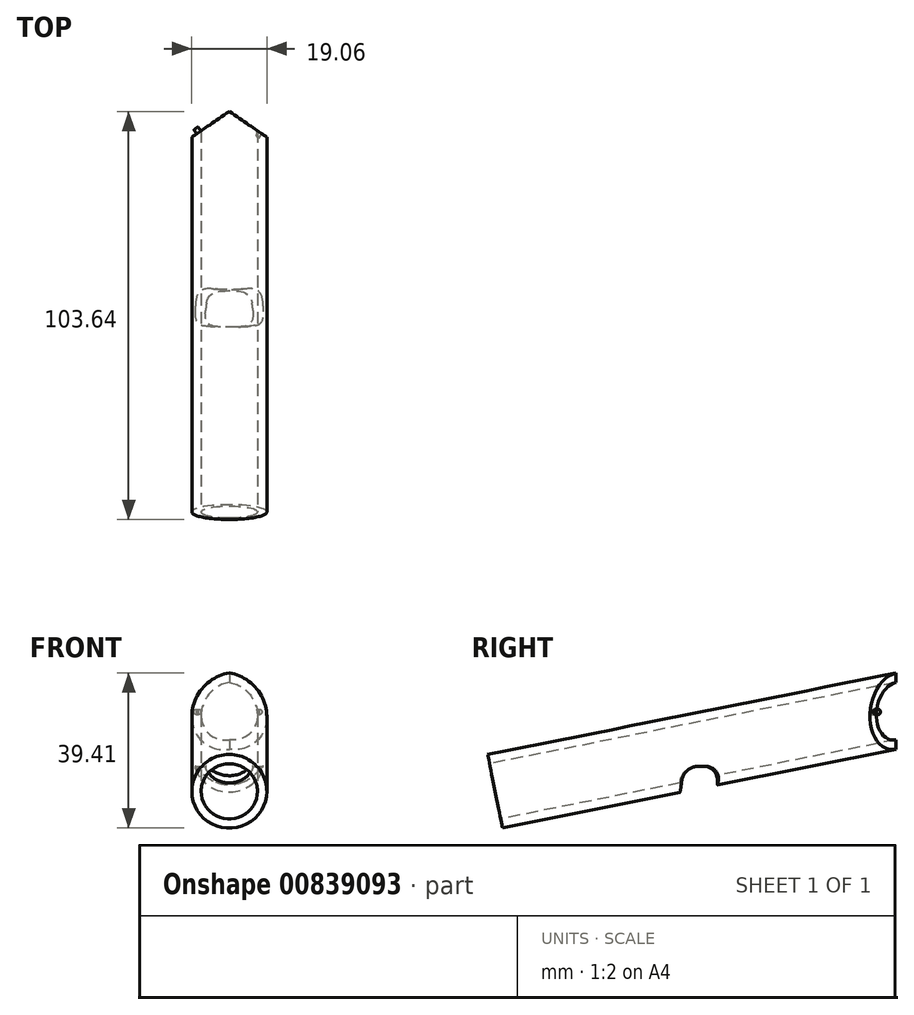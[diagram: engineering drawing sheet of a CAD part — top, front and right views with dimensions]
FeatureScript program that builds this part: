
annotation { "Feature Type Name" : "Feature", "Feature Type Description" : "" }
export const myFeature = defineFeature(function(context is Context, id is Id, definition is map)
    precondition{}
    {
        {
            var Q0;
            Q0=qCreatedBy(makeId("Front.planeOp"),FACE);
            var sketch = newSketch(context, id + "F0", { "sketchPlane" : qUnion([Q0])});
            skLineSegment(sketch, "E0", {"start": v(-25.47, 0) * mm, "end": v(29.78, 0) * mm});
            skSolve(sketch);
        }
        {
            var Q0;
            Q0=sQuery(id+"F0.wireOp",EDGE,"E0");
            cPlane(context, id + "F1", {"entities" : qUnion([Q0]), "cplaneType" : CPlaneType.LINE_ANGLE, "offset" : 25.4 * mm, "angle" : 11.3 * degree, "width" : 152.4 * mm, "height" : 152.4 * mm});
        }
        {
            var Q0;
            Q0=qCreatedBy(id+"F1.planeOp",FACE);
            var sketch = newSketch(context, id + "F2", { "sketchPlane" : qUnion([Q0])});
            skCircle(sketch, "E1", {"center": v(0, 0) * mm, "radius": 7.14 * mm});
            skCircle(sketch, "E2", {"center": v(0, 0) * mm, "radius": 9.53 * mm});
            skSolve(sketch);
        }
        {
            var Q0;
            Q0=makeQuery(id+"F2.imprint","IMPRINT",FACE,{"disambiguationData":[TD([[makeQuery(id+"F2.imprint","IMPRINT",EDGE,{"derivedFrom":sQuery(id+"F2.wireOp",EDGE,"E1")}),-1.0]])]});
            extrude(context, id + "F3", {"entities" : qUnion([Q0]), "depth" : 107.95 * mm, "offsetDistance" : 25.4 * mm});
        }
        {
            var Q0;
            Q0=qCreatedBy(makeId("Top.planeOp"),FACE);
            var sketch = newSketch(context, id + "F4", { "sketchPlane" : qUnion([Q0])});
            skLineSegment(sketch, "E3", {"start": v(0, 0) * mm, "end": v(0, 139.91) * mm, "construction": true});
            skLineSegment(sketch, "E4", {"start": v(-27.69, 95.25) * mm, "end": v(29.95, 95.25) * mm, "construction": true});
            skLineSegment(sketch, "E5", {"start": v(-9.52, 95.25) * mm, "end": v(-9.53, 133.35) * mm});
            skLineSegment(sketch, "E6", {"start": v(-9.53, 133.35) * mm, "end": v(9.52, 133.35) * mm});
            skLineSegment(sketch, "E7", {"start": v(9.52, 133.35) * mm, "end": v(9.52, 95.25) * mm});
            skLineSegment(sketch, "E8", {"start": v(0, 101.77) * mm, "end": v(-23.24, 85.86) * mm});
            skLineSegment(sketch, "E9", {"start": v(0, 101.77) * mm, "end": v(16.46, 90.5) * mm});
            skSolve(sketch);
        }
        {
            var Q0;
            Q0=qSketchRegion(id+"F4",true);
            extrude(context, id + "F5", {"entities" : qUnion([Q0]), "operationType" : NewBodyOperationType.REMOVE, "depth" : 127 * mm, "offsetDistance" : 25.4 * mm});
        }
        {
            var Q0;
            Q0=qCreatedBy(makeId("Right.planeOp"),FACE);
            var sketch = newSketch(context, id + "F6", { "sketchPlane" : qUnion([Q0])});
            skLineSegment(sketch, "E10", {"start": v(0, 0) * mm, "end": v(63.5, 0) * mm, "construction": true});
            skLineSegment(sketch, "E11", {"start": v(63.5, 0) * mm, "end": v(63.5, 10.16) * mm, "construction": true});
            skSolve(sketch);
        }
        {
            var Q0;
            Q0=qCreatedBy(makeId("Top.planeOp"),FACE);
            var sketch = newSketch(context, id + "F7", { "sketchPlane" : qUnion([Q0])});
            skCircle(sketch, "E12", {"center": v(0, 101.6) * mm, "radius": 54.61 * mm});
            skCircle(sketch, "E13", {"center": v(0, 101.6) * mm, "radius": 45.09 * mm});
            skSolve(sketch);
        }
        {
            var Q0;
            Q0=makeQuery(id+"F7.imprint","IMPRINT",FACE,{"disambiguationData":[TD([[makeQuery(id+"F7.imprint","IMPRINT",EDGE,{"derivedFrom":sQuery(id+"F7.wireOp",EDGE,"E12")}),1.0]])]});
            extrude(context, id + "F8", {"entities" : qUnion([Q0]), "operationType" : NewBodyOperationType.REMOVE, "depth" : 6.35 * mm, "offsetDistance" : 25.4 * mm, "hasSecondDirection" : true, "secondDirectionOppositeDirection" : true, "secondDirectionDepth" : 25.4 * mm});
        }
        {
            var Q0;
            Q0=makeQuery(id+"F8.boolean.opBoolean","COPY",EDGE,{"disambiguationData":[OD(0.0)],"derivedFrom":makeQuery(id+"F8.opExtrude","CAP_EDGE",EDGE,{"disambiguationData":[OSD([sQuery(id+"F7.wireOp",EDGE,"E13")])],"isStart":false})});
            var Q1;
            Q1=makeQuery(id+"F8.boolean.opBoolean","COPY",EDGE,{"disambiguationData":[OD(1.0)],"derivedFrom":makeQuery(id+"F8.opExtrude","CAP_EDGE",EDGE,{"disambiguationData":[OSD([sQuery(id+"F7.wireOp",EDGE,"E12")])],"isStart":false})});
            var Q2;
            Q2=makeQuery(id+"F8.boolean.opBoolean","COPY",EDGE,{"disambiguationData":[OD(1.0)],"derivedFrom":makeQuery(id+"F8.opExtrude","CAP_EDGE",EDGE,{"disambiguationData":[OSD([sQuery(id+"F7.wireOp",EDGE,"E13")])],"isStart":false})});
            var Q3;
            Q3=makeQuery(id+"F8.boolean.opBoolean","COPY",EDGE,{"disambiguationData":[OD(0.0)],"derivedFrom":makeQuery(id+"F8.opExtrude","CAP_EDGE",EDGE,{"disambiguationData":[OSD([sQuery(id+"F7.wireOp",EDGE,"E12")])],"isStart":false})});
            fillet(context, id + "F9", {"entities" : qUnion([Q0, Q1, Q2, Q3]), "radius" : 3.8 * mm, "tangentPropagation" : true, "allowEdgeOverflow" : false});
        }
        {
            var Q0;
            Q0=makeQuery(id+"F5.boolean.opBoolean","COPY",FACE,{"derivedFrom":makeQuery(id+"F5.opExtrude","SWEPT_FACE",FACE,{"disambiguationData":[OSD([sQuery(id+"F4.wireOp",EDGE,"E9")])]})});
            var sketch = newSketch(context, id + "F10", { "sketchPlane" : qUnion([Q0])});
            skCircle(sketch, "E14", {"center": v(48.1, 20.17) * mm, "radius": 0.64 * mm});
            skSolve(sketch);
        }
        {
            var Q0;
            Q0=makeQuery(id+"F10.imprint","IMPRINT",FACE,{"disambiguationData":[TD([[makeQuery(id+"F10.imprint","IMPRINT",EDGE,{"derivedFrom":sQuery(id+"F10.wireOp",EDGE,"E14")}),1.0]])]});
            extrude(context, id + "F11", {"entities" : qUnion([Q0]), "operationType" : NewBodyOperationType.REMOVE, "oppositeDirection" : true, "depth" : 1.27 * mm, "offsetDistance" : 25.4 * mm});
        }
        {
            var Q0;
            Q0=makeQuery(id+"F5.boolean.opBoolean","COPY",FACE,{"derivedFrom":makeQuery(id+"F5.opExtrude","SWEPT_FACE",FACE,{"disambiguationData":[OSD([sQuery(id+"F4.wireOp",EDGE,"E8")])]})});
            var sketch = newSketch(context, id + "F12", { "sketchPlane" : qUnion([Q0])});
            skCircle(sketch, "E15", {"center": v(-48.1, 20.17) * mm, "radius": 0.64 * mm});
            skSolve(sketch);
        }
        {
            var Q0;
            Q0=makeQuery(id+"F12.imprint","IMPRINT",FACE,{"disambiguationData":[TD([[makeQuery(id+"F12.imprint","IMPRINT",EDGE,{"derivedFrom":sQuery(id+"F12.wireOp",EDGE,"E15")}),1.0]])]});
            extrude(context, id + "F13", {"entities" : qUnion([Q0]), "operationType" : NewBodyOperationType.ADD, "depth" : 1.27 * mm, "offsetDistance" : 25.4 * mm});
        }
    });
